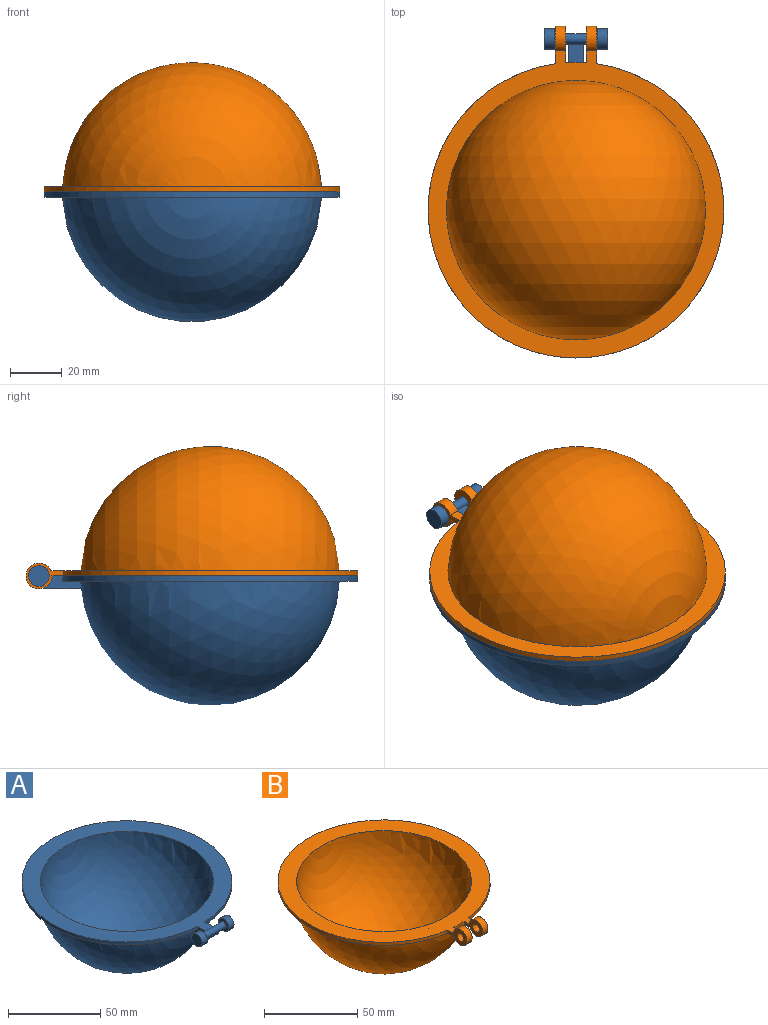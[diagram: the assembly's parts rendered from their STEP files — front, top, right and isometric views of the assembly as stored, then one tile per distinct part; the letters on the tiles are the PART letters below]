
ASSEMBLY  parts=2 mates=1
PART A: 16 faces, bbox 114x127x60.8 mm
  f0: plane 121x114mm, normal (0,0,1), area 3309.4mm2, adj f1,f2,f5,f6,f7
  f1: sphere r=47mm, area 13879.6mm2, adj f0
  f2: cylinder r=57mm len=114mm, axis (0,0,1), area 704.3mm2, adj f0,f3,f5,f6
  f3: plane 114x113.92mm, normal (0,0,-1), area 2323.4mm2, adj f2,f4,f5,f6
  f4: sphere r=50mm, area 15033.6mm2, adj f3,f5,f6,f14
  f5: plane 17.84x5mm, normal (1,0,0), area 63.9mm2, adj f0,f2,f3,f4,f7,f14,f15
  f6: plane 17.84x5mm, normal (-1,0,0), area 63.9mm2, adj f0,f2,f3,f4,f7,f14,f15
  f7: cylinder r=2mm len=16.5mm, axis (-1,0,0), area 178.3mm2, adj f0,f5,f6,f10,f13,f15
  f8: cylinder r=4mm len=8mm, axis (-1,0,0), area 100.5mm2, adj f9,f10
  f9: plane 8x8mm, normal (1,0,0), area 50.3mm2, adj f8
  f10: plane 8x8mm, normal (-1,0,0), area 37.7mm2, adj f7,f8
  f11: cylinder r=4mm len=8mm, axis (1,0,0), area 100.5mm2, adj f12,f13
  f12: plane 8x8mm, normal (-1,0,0), area 50.3mm2, adj f11
  f13: plane 8x8mm, normal (1,0,0), area 37.7mm2, adj f7,f11
  f14: plane 13.02x6mm, normal (0,0,-1), area 77.8mm2, adj f4,f5,f6,f15
  f15: cylinder r=5mm len=6mm, axis (-1,0,0), area 39.1mm2, adj f5,f6,f7,f14
PART B: 14 faces, bbox 114x128x78.1 mm
  f0: plane 14.56x10mm, normal (-1,0,0), area 68.3mm2, adj f2,f3,f6,f12,f13
  f1: plane 14.14x10mm, normal (1,0,0), area 67.5mm2, adj f2,f3,f4,f12,f13
  f2: plane 118x114mm, normal (0,0,1), area 3301.9mm2, adj f0,f1,f4,f5,f6,f8,f9,f11
  f3: plane 118.42x114mm, normal (0,0,-1), area 2403.6mm2, adj f0,f1,f4,f6,f7,f8,f9,f11
  f4: cylinder r=57mm len=8mm, axis (0,0,1), area 16mm2, adj f1,f2,f3,f9
  f5: sphere r=47mm, area 13879.6mm2, adj f2
  f6: cylinder r=57mm len=114mm, axis (0,0,1), area 684.2mm2, adj f0,f2,f3,f8
  f7: sphere r=50mm, area 15082.8mm2, adj f3
  f8: plane 14.56x10mm, normal (1,0,0), area 68.3mm2, adj f2,f3,f6,f10,f11
  f9: plane 14.14x10mm, normal (-1,0,0), area 67.5mm2, adj f2,f3,f4,f10,f11
  f10: cylinder r=2.5mm len=5mm, axis (1,0,0), area 62.8mm2, adj f8,f9
  f11: cylinder r=5mm len=10mm, axis (1,0,0), area 117.4mm2, adj f2,f3,f8,f9
  f12: cylinder r=2.5mm len=5mm, axis (-1,0,0), area 62.8mm2, adj f0,f1
  f13: cylinder r=5mm len=10mm, axis (-1,0,0), area 117.4mm2, adj f0,f1,f2,f3
PLACE A rot(axis=(0,0,1),180deg) t=(132.44,-222.63,-148.77)mm
PLACE B rot(axis=(1,0,0),180deg) t=(132.44,-222.63,-148.77)mm
MATE revolute A.f7 <-> B.f11  axis (1,0,0) through (124.19,-156.63,-148.77)mm
